AUTODESK INVENTOR PART (.ipt)
format: ipt  version: 2017 (Build 210142000, 142)  size: 211,456 bytes
history: native  units: in
note: dims shown in document units (in); Inventor stores cm internally (conversion verified against a paired STEP export)
features: extrude x8, sketch x8, projected_geometry x2, hole x1
ambient origin geometry x8: Origin, YZ Plane, XZ Plane, XY Plane, X Axis, Y Axis, Z Axis, Center Point
bodies: Solid1 (feature_tree)
feature tree (19):
  extrude  "Extrusion1"  Depth=2.5945in
  hole  "Hole1"  [1 undecoded]
  extrude  "Extrusion2"  Depth=0.1575in
  extrude  "Extrusion3"  Depth=0.1575in
  extrude  "Extrusion4"  Depth=0.9055in
  extrude  "Extrusion5"  Depth=0.112in
  extrude  "Extrusion6"  Depth=0.1in
  extrude  "Extrusion7"  Depth=0.1in
  extrude  "Extrusion8"  Depth=0.2in TaperAngle=0.0deg
  sketch  "Sketch1"  dims[d0=2.1378in d1=2.5945in]
  sketch  "Sketch2"  dims[d2=0.063in d3=0.0in d4=0.1654in]
  sketch  "Sketch3"  dims[d5=0.1693in d6=0.1575in]
  sketch  "Sketch4"  dims[d7=0.1654in d8=0.1575in]
  projected_geometry  "Projected Loop1"
  sketch  "Sketch5"  dims[d9=0.1693in]
  sketch  "Sketch7"  dims[d10=0.125in d11=0.75in d12=0.375in d13=0.25in d14=0.5635in d15=1.0in d16=0.8108in d17=0.9055in]
  sketch  "Sketch9"  dims[d18=2.0079in d19=0.112in]
  sketch  "Sketch10"  dims[d20=0.032in d21=0.1in d22=0.1in d23=0.2in d24=0.0in d25=0.063in d26=0.0in d27=0.315in d28=0.315in d30=0.252in d31=0.0in d32=0.2in d33=0.2992in d34=0.6811in d35=0.04in d36=0.0984in d37=0.0in d39=0.315in d40=0.4488in d41=0.035in d43=0.315in d44=0.128in d45=0.035in d46=0.2165in d47=0.0in d48=0.49in d49=0.072in d50=0.342in d51=0.027in d52=0.2165in d53=0.0in d54=1.745in d55=0.463in d56=0.952in d57=0.484in d58=0.04in d59=0.0in d60=0.5906in d61=1.563in]
  projected_geometry  "Projected Loop2"
note: 1 required parameter value undecoded (feature->parameter linkage not recoverable at this tier; creation-order binding heuristic only, values carry confidence <= 0.55)
